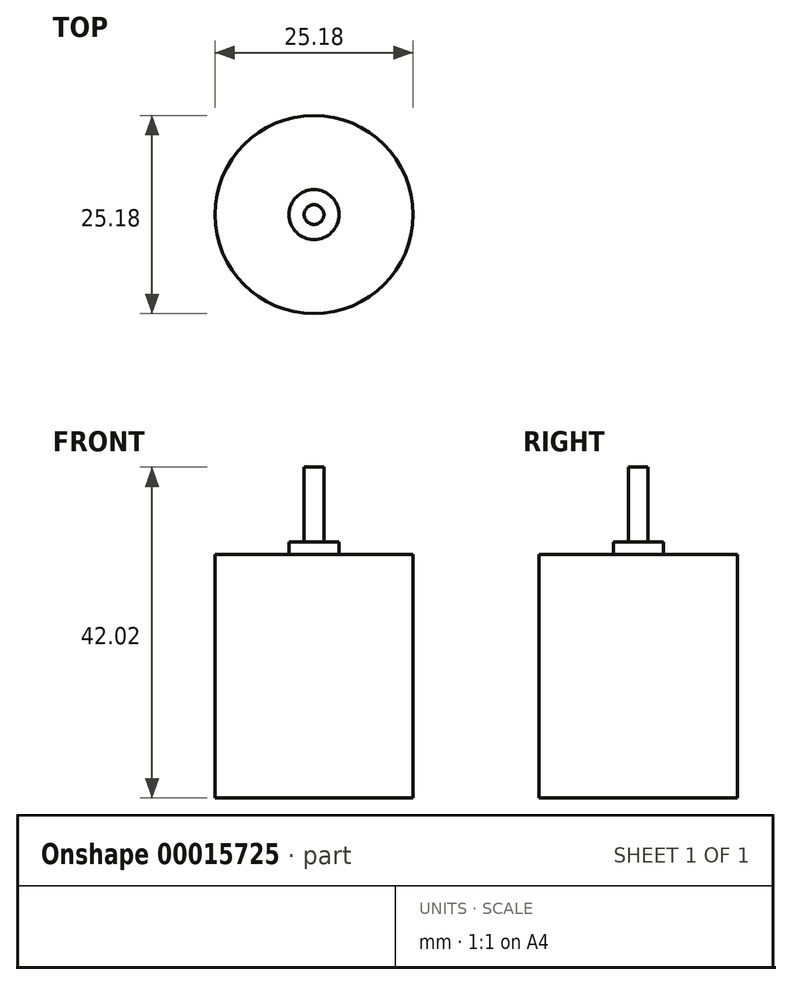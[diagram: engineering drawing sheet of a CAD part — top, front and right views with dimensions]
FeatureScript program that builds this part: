
annotation { "Feature Type Name" : "Feature", "Feature Type Description" : "" }
export const myFeature = defineFeature(function(context is Context, id is Id, definition is map)
    precondition{}
    {
        {
            var Q0;
            Q0=qCreatedBy(makeId("Top.planeOp"),FACE);
            var sketch = newSketch(context, id + "F0", { "sketchPlane" : qUnion([Q0])});
            skCircle(sketch, "E0", {"center": v(0, 0) * mm, "radius": 12.59 * mm});
            skSolve(sketch);
        }
        {
            var Q0;
            Q0 = qSketchRegion(id + "F0", true);
            extrude(context, id + "F1", {"entities" : qUnion([Q0]), "depth" : 30.91 * mm});
        }
        {
            var Q0;
            Q0=makeQuery(id+"F1.opExtrude","CAP_FACE",FACE,{"disambiguationData":[OSD([sQuery(id+"F0.wireOp",EDGE,"E0")])],"isStart":false});
            var sketch = newSketch(context, id + "F2", { "sketchPlane" : qUnion([Q0])});
            skCircle(sketch, "E1", {"center": v(0, 0) * mm, "radius": 3.18 * mm});
            skSolve(sketch);
        }
        {
            var Q0;
            Q0 = qSketchRegion(id + "F2", true);
            extrude(context, id + "F3", {"entities" : qUnion([Q0]), "operationType" : NewBodyOperationType.ADD, "depth" : 1.59 * mm});
        }
        {
            var Q0;
            Q0=makeQuery(id+"F3.opExtrude","CAP_FACE",FACE,{"disambiguationData":[OSD([sQuery(id+"F2.wireOp",EDGE,"E1")])],"isStart":false});
            var sketch = newSketch(context, id + "F4", { "sketchPlane" : qUnion([Q0])});
            skCircle(sketch, "E2", {"center": v(0, 0) * mm, "radius": 1.25 * mm});
            skSolve(sketch);
        }
        {
            var Q0;
            Q0 = qSketchRegion(id + "F4", true);
            extrude(context, id + "F5", {"entities" : qUnion([Q0]), "operationType" : NewBodyOperationType.ADD, "depth" : 9.52 * mm});
        }
    });
